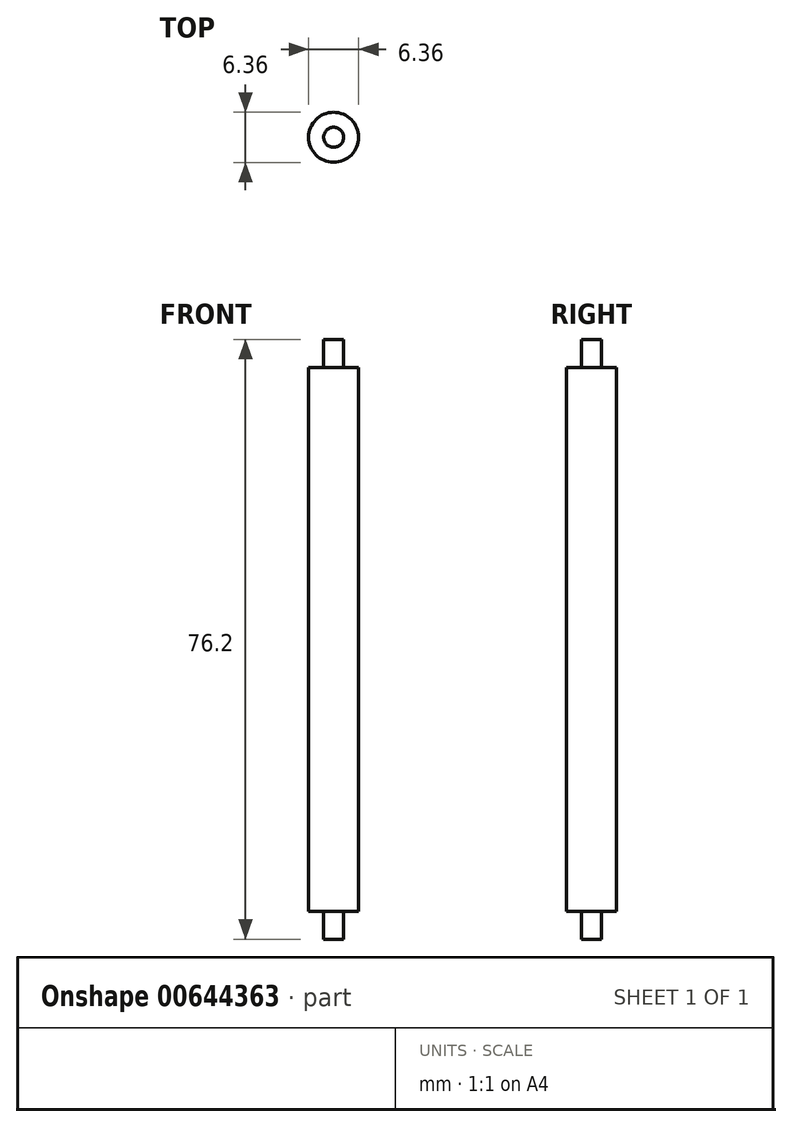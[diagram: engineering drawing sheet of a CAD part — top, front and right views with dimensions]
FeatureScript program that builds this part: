
annotation { "Feature Type Name" : "Feature", "Feature Type Description" : "" }
export const myFeature = defineFeature(function(context is Context, id is Id, definition is map)
    precondition{}
    {
        {
            var Q0;
            Q0=qCreatedBy(makeId("Front.planeOp"),FACE);
            var sketch = newSketch(context, id + "F0", { "sketchPlane" : qUnion([Q0])});
            skLineSegment(sketch, "E0.left", {"start": v(0, 0) * mm, "end": v(0, 69.09) * mm});
            skLineSegment(sketch, "E0.right", {"start": v(-3.18, 0) * mm, "end": v(-3.18, 69.09) * mm});
            skLineSegment(sketch, "E1.top", {"start": v(0, 72.64) * mm, "end": v(-1.27, 72.64) * mm});
            skLineSegment(sketch, "E1.left", {"start": v(0, 69.09) * mm, "end": v(0, 72.64) * mm});
            skLineSegment(sketch, "E1.right", {"start": v(-1.27, 69.09) * mm, "end": v(-1.27, 72.64) * mm});
            skLineSegment(sketch, "E2.top", {"start": v(0, -3.56) * mm, "end": v(-1.27, -3.56) * mm});
            skLineSegment(sketch, "E2.left", {"start": v(0, 0) * mm, "end": v(0, -3.56) * mm});
            skLineSegment(sketch, "E2.right", {"start": v(-1.27, 0) * mm, "end": v(-1.27, -3.56) * mm});
            skLineSegment(sketch, "E3", {"start": v(-3.18, 0) * mm, "end": v(-1.27, 0) * mm});
            skLineSegment(sketch, "E4", {"start": v(-3.18, 69.09) * mm, "end": v(-1.27, 69.09) * mm});
            skSolve(sketch);
        }
        {
            var Q0;
            Q0=makeQuery(id+"F0.imprint","IMPRINT",FACE,{"disambiguationData":[TD([[makeQuery(id+"F0.imprint","IMPRINT",EDGE,{"derivedFrom":sQuery(id+"F0.wireOp",EDGE,"E0.left")}),1.0]])]});
            var Q1;
            Q1=sQuery(id+"F0.wireOp",EDGE,"E0.left");
            revolve(context, id + "F1", {"entities" : qUnion([Q0]), "axis" : qUnion([Q1]), "revolveType" : RevolveType.FULL});
        }
    });
